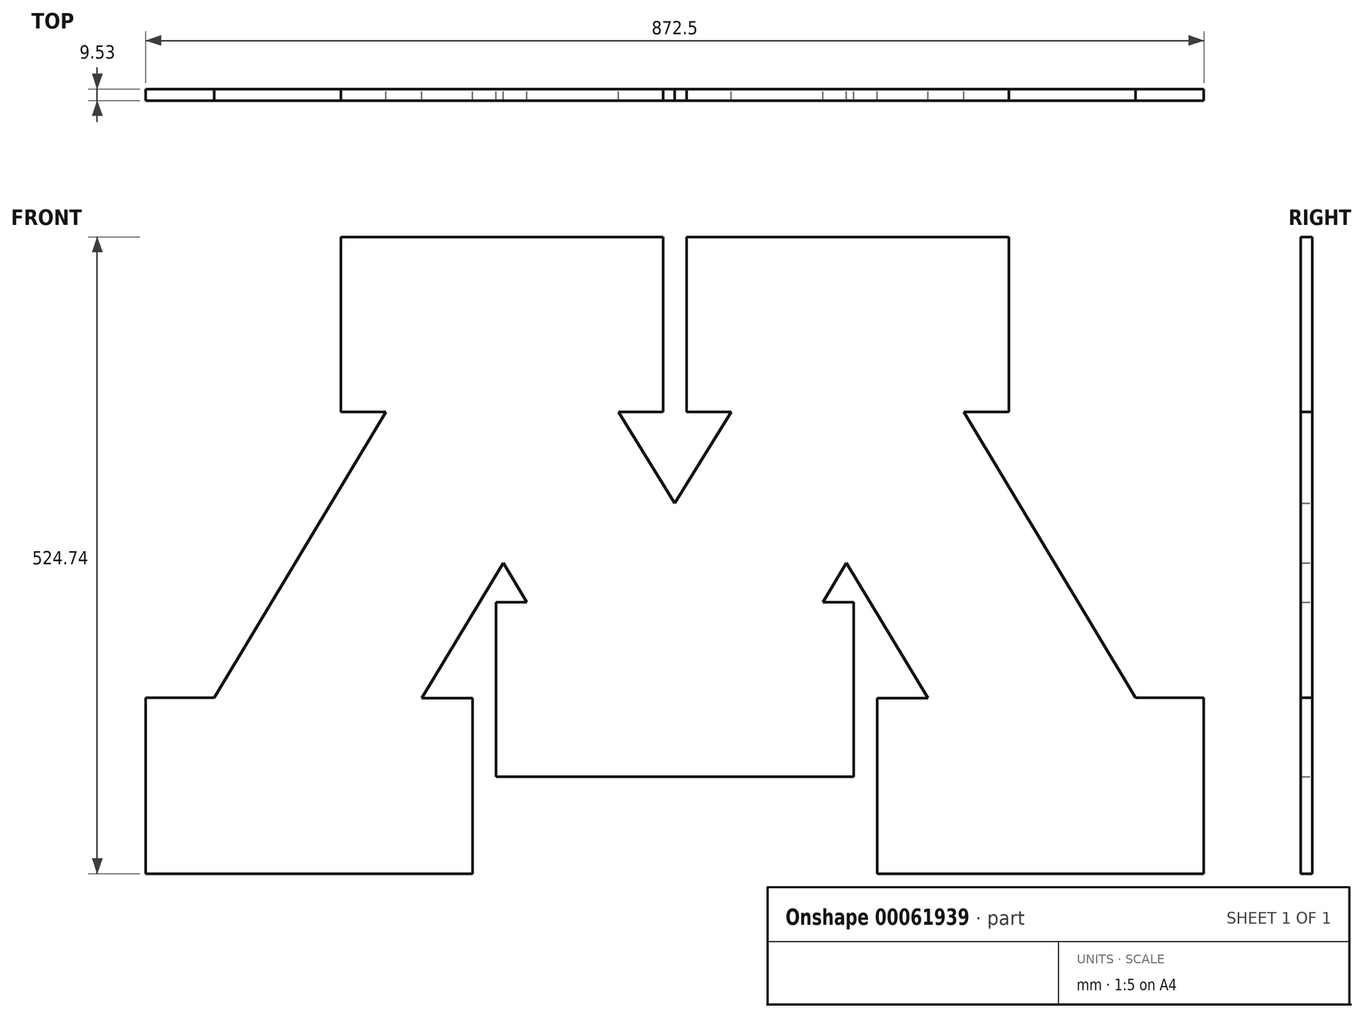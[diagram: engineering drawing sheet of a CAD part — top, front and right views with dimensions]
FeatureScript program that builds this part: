
annotation { "Feature Type Name" : "Feature", "Feature Type Description" : "" }
export const myFeature = defineFeature(function(context is Context, id is Id, definition is map)
    precondition{}
    {
        {
            var Q0;
            Q0=qCreatedBy(makeId("Front.planeOp"),FACE);
            var sketch = newSketch(context, id + "F0", { "sketchPlane" : qUnion([Q0])});
            skLineSegment(sketch, "E0", {"start": v(0, 42.9) * mm, "end": v(46.43, 118.22) * mm});
            skLineSegment(sketch, "E1", {"start": v(46.43, 118.22) * mm, "end": v(9.64, 118.22) * mm});
            skLineSegment(sketch, "E2", {"start": v(9.64, 118.22) * mm, "end": v(9.64, 262.37) * mm});
            skLineSegment(sketch, "E3", {"start": v(9.64, 262.37) * mm, "end": v(275.35, 262.37) * mm});
            skLineSegment(sketch, "E4", {"start": v(275.35, 262.37) * mm, "end": v(275.35, 118.22) * mm});
            skLineSegment(sketch, "E5", {"start": v(275.35, 118.22) * mm, "end": v(238.42, 118.22) * mm});
            skLineSegment(sketch, "E6", {"start": v(238.42, 118.22) * mm, "end": v(379.85, -117.5) * mm});
            skLineSegment(sketch, "E7", {"start": v(379.85, -117.5) * mm, "end": v(436.25, -117.5) * mm});
            skLineSegment(sketch, "E8", {"start": v(436.25, -117.5) * mm, "end": v(436.25, -262.37) * mm});
            skLineSegment(sketch, "E9", {"start": v(436.25, -262.37) * mm, "end": v(166.75, -262.37) * mm});
            skLineSegment(sketch, "E10", {"start": v(166.75, -262.37) * mm, "end": v(166.75, -117.68) * mm});
            skLineSegment(sketch, "E11", {"start": v(166.75, -117.68) * mm, "end": v(208.64, -117.68) * mm});
            skLineSegment(sketch, "E12", {"start": v(208.64, -117.68) * mm, "end": v(141.3, -6.35) * mm});
            skLineSegment(sketch, "E13", {"start": v(141.3, -6.35) * mm, "end": v(122.03, -38.53) * mm});
            skLineSegment(sketch, "E14", {"start": v(122.03, -38.53) * mm, "end": v(147.46, -38.53) * mm});
            skLineSegment(sketch, "E15", {"start": v(147.46, -38.53) * mm, "end": v(147.46, -182.45) * mm});
            skLineSegment(sketch, "E16", {"start": v(147.46, -182.45) * mm, "end": v(-147.46, -182.45) * mm});
            skLineSegment(sketch, "E17", {"start": v(-147.46, -182.45) * mm, "end": v(-147.46, -38.53) * mm});
            skLineSegment(sketch, "E18", {"start": v(-147.46, -38.53) * mm, "end": v(-122.03, -38.53) * mm});
            skLineSegment(sketch, "E19", {"start": v(-122.03, -38.53) * mm, "end": v(-141.3, -6.35) * mm});
            skLineSegment(sketch, "E20", {"start": v(-141.3, -6.35) * mm, "end": v(-208.64, -117.68) * mm});
            skLineSegment(sketch, "E21", {"start": v(-208.64, -117.68) * mm, "end": v(-166.75, -117.68) * mm});
            skLineSegment(sketch, "E22", {"start": v(-166.75, -117.68) * mm, "end": v(-166.75, -262.37) * mm});
            skLineSegment(sketch, "E23", {"start": v(-166.75, -262.37) * mm, "end": v(-436.25, -262.37) * mm});
            skLineSegment(sketch, "E24", {"start": v(-436.25, -262.37) * mm, "end": v(-436.25, -117.5) * mm});
            skLineSegment(sketch, "E25", {"start": v(-436.25, -117.5) * mm, "end": v(-379.85, -117.5) * mm});
            skLineSegment(sketch, "E26", {"start": v(-379.85, -117.5) * mm, "end": v(-238.42, 118.22) * mm});
            skLineSegment(sketch, "E27", {"start": v(-238.42, 118.22) * mm, "end": v(-275.35, 118.22) * mm});
            skLineSegment(sketch, "E28", {"start": v(-275.35, 118.22) * mm, "end": v(-275.35, 262.37) * mm});
            skLineSegment(sketch, "E29", {"start": v(-275.35, 262.37) * mm, "end": v(-9.64, 262.37) * mm});
            skLineSegment(sketch, "E30", {"start": v(-9.64, 262.37) * mm, "end": v(-9.64, 118.22) * mm});
            skLineSegment(sketch, "E31", {"start": v(-9.64, 118.22) * mm, "end": v(-46.43, 118.22) * mm});
            skLineSegment(sketch, "E32", {"start": v(-46.43, 118.22) * mm, "end": v(0, 42.9) * mm});
            skSolve(sketch);
        }
        {
            var Q0;
            Q0=makeQuery(id+"F0.imprint","IMPRINT",FACE,{"disambiguationData":[TD([[makeQuery(id+"F0.imprint","IMPRINT",EDGE,{"derivedFrom":sQuery(id+"F0.wireOp",EDGE,"E0")}),-1.0]])]});
            extrude(context, id + "F1", {"entities" : qUnion([Q0]), "depth" : 9.52 * mm});
        }
    });
